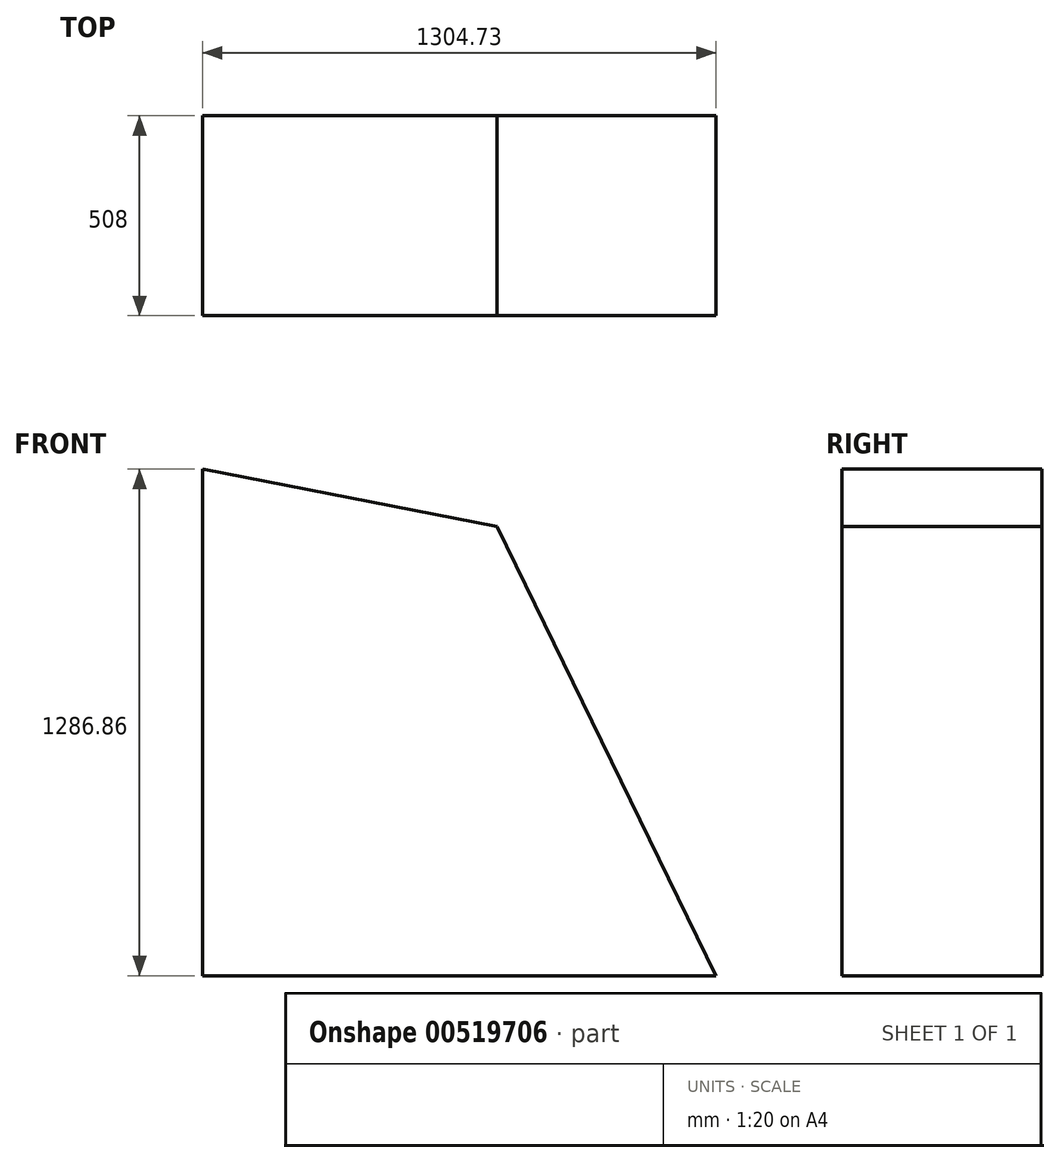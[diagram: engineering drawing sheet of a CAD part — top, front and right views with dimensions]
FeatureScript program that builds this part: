
annotation { "Feature Type Name" : "Feature", "Feature Type Description" : "" }
export const myFeature = defineFeature(function(context is Context, id is Id, definition is map)
    precondition{}
    {
        {
            var Q0;
            Q0=qCreatedBy(makeId("Front.planeOp"),FACE);
            var sketch = newSketch(context, id + "F0", { "sketchPlane" : qUnion([Q0])});
            skLineSegment(sketch, "E0", {"start": v(-1185.8, 0) * mm, "end": v(118.92, 0) * mm});
            skLineSegment(sketch, "E1", {"start": v(118.92, 0) * mm, "end": v(-437.8, 1141.47) * mm});
            skLineSegment(sketch, "E2", {"start": v(-437.8, 1141.47) * mm, "end": v(-1185.8, 1286.86) * mm});
            skLineSegment(sketch, "E3", {"start": v(-1185.8, 1286.86) * mm, "end": v(-1185.8, 0) * mm});
            skSolve(sketch);
        }
        {
            var Q0;
            Q0=makeQuery(id+"F0.imprint","IMPRINT",FACE,{"disambiguationData":[TD([[makeQuery(id+"F0.imprint","IMPRINT",EDGE,{"derivedFrom":sQuery(id+"F0.wireOp",EDGE,"E0")}),1.0]])]});
            extrude(context, id + "F1", {"entities" : qUnion([Q0]), "depth" : 508 * mm, "offsetDistance" : 25.4 * mm});
        }
    });
